# Revit family: Remote_Chiller-Murdock-A9100080-A_Series
name_source: partatom
category: Mechanical Equipment
units: mm (PartAtom-declared; Revit-internal decimal feet)

## family parameters
Cut with Voids When Loaded = No
Host = Face
OmniClass Number = 23.65.35.11.11
OmniClass Title = Storage Water Heaters
Part Type = Normal
Room Calculation Point = No
Round Connector Dimension = Use Diameter
Shared = Yes

## types (2) — shared parameters
-220V 220 volt / 50Hz compressor = No
-LG Louvered grille - Granite Powder Coated = No
-LG1Accessory Louvered Grille = No
-SRC Shelf for remote chiller = No
ADA Compliant = Yes
Assembly Code = D3030100
Chiller Option = 8.0 GPH
Cold Water Connection Diameter = 3/8"
Compliance Certifications = ANSI/ASHRAE 18, IAPMO tested to NSF/ANSI 61, Section 9, UL Listed (US and Canada), Lead-Free Federal Law 111-380, CE complaint for 220 V electrical
Connection Length = 1 3/4"
Default Elevation = 0"
Description = 8 GPH Remote Chiller for Refrigerated Drinking Fountains
Finish = Steel-Murdock-Galvanized
Full Load Amps = 5 VA
Height = 19"
Length = 15 5/8"
Manufacturer = Murdock Mfg.
Material = Steel-Murdock-Galvanized
Product Documentation Link = https://www.murdockmfg.com
Product Page URL = https://www.murdockmfg.com
Rated Watts = 390
Shipping Weight = 43 lb
URL = https://www.murdockmfg.com
Voltage = 115 V
Width = 10 1/8"
cUPC Compliant = Yes

## per-type parameters (varying)
| type | Power |
| A9100080-A | 120V (Standard U.S. electrical) |
| A9100080-220V-A | 220 volt / 50Hz compressor |

note: column(s) folded — value = type name in every type: Model

## geometry (parser evidence)
native form markers: Sweep x2
no freeform markers — native parametric forms only
